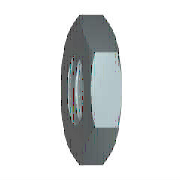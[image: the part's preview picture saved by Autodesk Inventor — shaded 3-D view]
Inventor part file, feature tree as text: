
AUTODESK INVENTOR PART (.ipt)
format: ipt  version: 2015 (Build 190159000, 159)  size: 163,328 bytes
history: native  units: mm (DEFAULTED — no unit token found)
features: sketch x3, chamfer x1, hole x1, other x1, plane x1
ambient origin geometry x7: Origin, YZ Plane, XZ Plane, X Axis, Y Axis, Z Axis, Center Point
bodies: Solid1 (feature_tree), Body (feature_tree)
feature tree (7):
  chamfer  "Chamfer1"  Angle=30.0deg  [1 undecoded]
  hole  "Thread"  [1 undecoded]
  other  "Work Axis1"
  plane  "Work Plane1"
  sketch  "Sketch1"  dims[d0=18.475209mm]
  sketch  "Sketch2"  dims[d1=5.0mm]
  sketch  "Sketch3"  dims[d2=0.0mm d3=30.0deg d4=30.0deg d5=14.63mm d6=14.63mm d7=90.0deg d25=8.917468mm d26=6.0mm d27=4.0mm d28=2.0mm d29=14.3117mm d30=8.0mm d31=20.594885mm d8=0.541266mm d9=30.0deg d10=0.541266mm d11=30.0deg d13=0.0mm d14=0.0mm d39=0.0mm d40=0.541266mm d41=0.541266mm d42=0.0mm]
note: 2 required parameter values undecoded (feature->parameter linkage not recoverable at this tier; creation-order binding heuristic only, values carry confidence <= 0.55)
